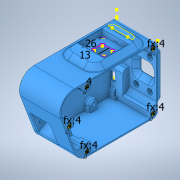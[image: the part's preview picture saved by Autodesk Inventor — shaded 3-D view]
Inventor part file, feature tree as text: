
AUTODESK INVENTOR PART (.ipt)
format: ipt  version: 2021.1 (Build 251245010, 245A)  size: 1,524,224 bytes
history: mixed  units: in
note: dims shown in document units (in); Inventor stores cm internally (conversion verified against a paired STEP export)
features: extrude x17, sketch x14, projected_geometry x5, direct_edit x2, other x2, chamfer x1, move_body x1, imported_body x1
ambient origin geometry x8: Origin, YZ Plane, XZ Plane, XY Plane, X Axis, Y Axis, Z Axis, Center Point
bodies: Solid1 (imported_parasolid), Body1 (imported_parasolid)
feature tree (43):
  sketch  "Skizze1"  dims[d0=0.1575in d1=0.1575in]
  extrude  "Extrusion2"  Depth=0.1575in
  extrude  "Extrusion1"  Depth=0.1575in
  sketch  "Skizze3"  dims[d2=0.1575in d3=0.1575in]
  extrude  "Extrusion3"  Depth=0.1575in TaperAngle=0.0deg
  extrude  "Extrusion4"  Depth=0.2756in TaperAngle=0.0deg
  extrude  "Extrusion5"  Depth=0.1575in
  extrude  "Extrusion6"  Depth=0.1575in
  direct_edit  "Direktbearbeitung2"
  extrude  "Extrusion7"  Depth=0.315in
  extrude  "Extrusion8"  Depth=0.1969in TaperAngle=0.0deg
  direct_edit  "Direktbearbeitung3"
  extrude  "Extrusion9"  Depth=0.1575in
  extrude  "Extrusion10"  Depth=0.1575in
  extrude  "Extrusion11"  Depth=0.315in
  sketch  "Skizze11"  dims[d26=0.1575in d27=0.1575in]
  extrude  "Extrusion12"  Depth=0.3937in TaperAngle=0.0deg
  extrude  "Extrusion13"  Depth=0.0079in TaperAngle=0.0deg
  extrude  "Extrusion14"  TaperAngle=135.0deg  [1 undecoded]
  extrude  "Extrusion15"  Depth=0.3937in TaperAngle=0.0deg
  extrude  "Extrusion16"  Depth=0.3937in TaperAngle=0.0deg
  sketch  "Skizze14"  dims[d36=0.0in d37=0.0in d38=-0.0394in d39=0.0079in d40=0.0in]
  extrude  "Extrusion18"  Depth=0.0394in TaperAngle=0.0deg
  chamfer  "Fase1"  Distance=0.0591in
  projected_geometry  "Projizierte Kontur2"
  sketch  "Skizze4"  dims[d4=0.1575in d5=0.252in d6=0.0in]
  sketch  "Skizze5"  dims[d7=0.2362in d8=0.0in d9=0.2756in d10=0.0in]
  sketch  "Skizze6"  dims[d11=0.1575in d12=0.0in d13=0.1575in]
  sketch  "Skizze7"  dims[d14=0.1575in d15=0.1575in]
  sketch  "Skizze8"  dims[d16=0.252in d17=0.0in d18=0.315in]
  sketch  "Skizze9"  dims[d19=45.0deg d20=0.1969in d21=0.5906in d22=0.0in d23=0.0in]
  sketch  "Skizze10"  dims[d24=0.1575in d25=0.1575in]
  projected_geometry  "Projizierte Kontur3"
  projected_geometry  "Projizierte Kontur4"
  projected_geometry  "Projizierte Kontur5"
  projected_geometry  "Projizierte Kontur6"
  sketch  "Skizze12"  dims[d28=0.252in d29=0.0in d30=0.315in]
  sketch  "Skizze13"  dims[d31=135.0deg d32=0.3937in d33=0.1772in d34=0.0in d35=0.0in]
  sketch  "Skizze15"  dims[d41=0.315in d42=135.0deg d43=0.3937in d44=0.0in d45=0.3937in d46=0.0in d47=0.0394in d48=0.0in d49=0.0591in d50=0.0in d51=0.2756in d52=135.0deg d53=0.1969in d54=0.0in d55=0.2165in d56=0.1969in d57=0.0in d58=0.0394in d59=0.0in d62=0.3937in d63=0.0in d64=0.1969in d65=0.3937in d66=45.0deg d67=0.5118in d68=1.0236in]
  other  "Löschen2"
  other  "Löschen3"
  move_body  "Verschieben1"
  imported_body  NMx_Import_Brep_tag  [imported B-rep: ~72 faces, bbox_mm=[43.5, 17.0, 67.207107]]
note: 1 required parameter value undecoded (feature->parameter linkage not recoverable at this tier; creation-order binding heuristic only, values carry confidence <= 0.55)
